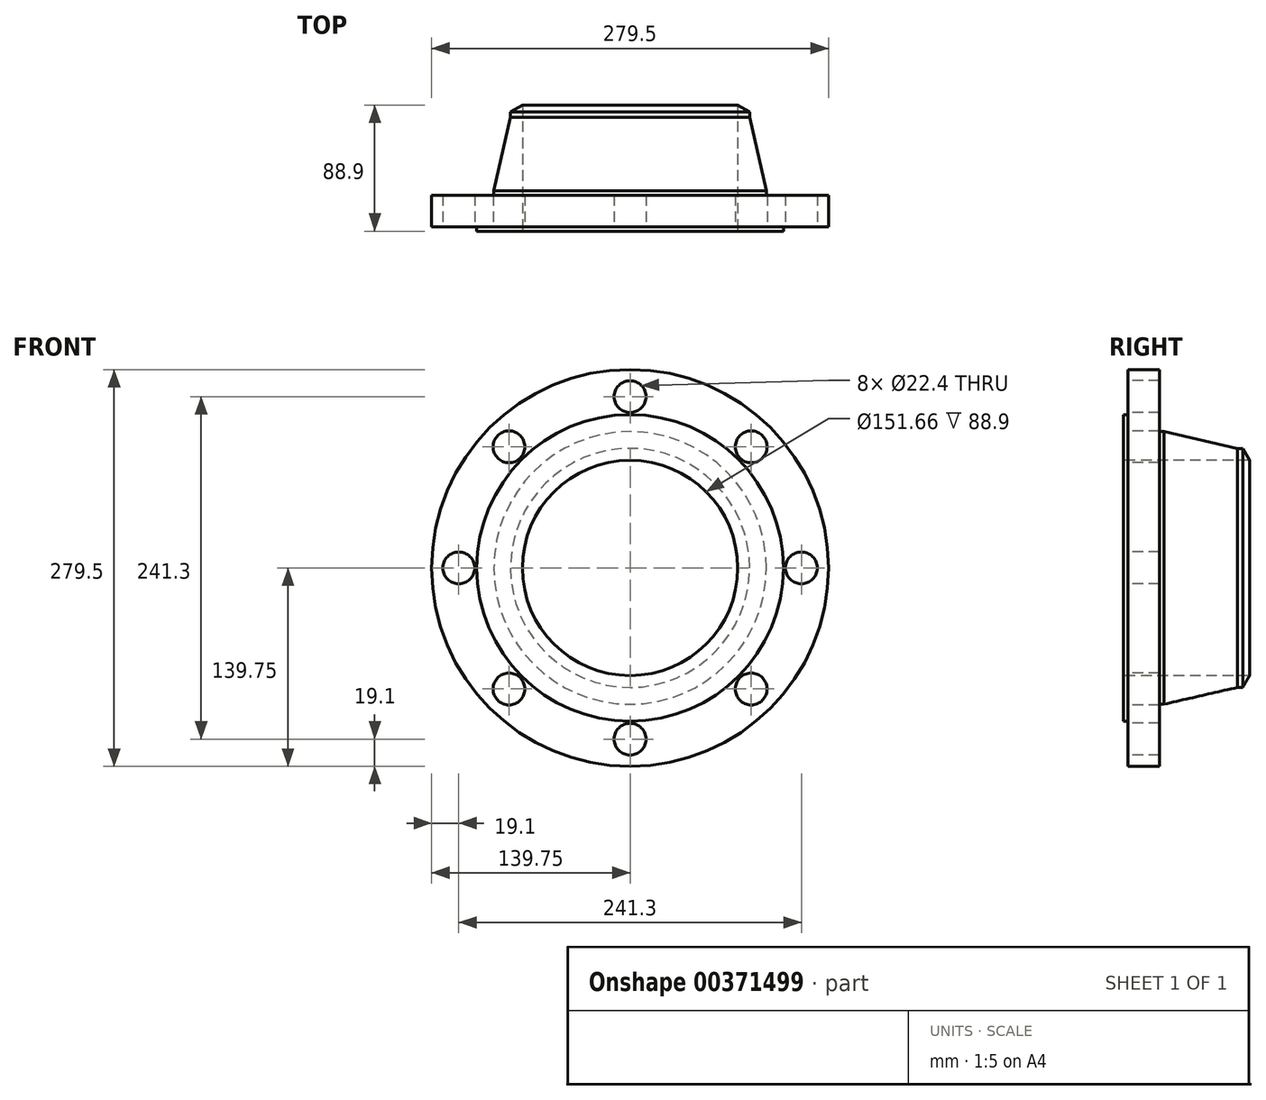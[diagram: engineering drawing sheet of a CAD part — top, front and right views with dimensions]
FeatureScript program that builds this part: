
annotation { "Feature Type Name" : "Feature", "Feature Type Description" : "" }
export const myFeature = defineFeature(function(context is Context, id is Id, definition is map)
    precondition{}
    {
        {
            var Q0;
            Q0=qCreatedBy(makeId("Right.planeOp"),FACE);
            var sketch = newSketch(context, id + "F0", { "sketchPlane" : qUnion([Q0])});
            skLineSegment(sketch, "E0", {"start": v(-100.01, 0) * mm, "end": v(99.5, 0) * mm, "construction": true});
            skLineSegment(sketch, "E1", {"start": v(0, 75.83) * mm, "end": v(0, 107.95) * mm});
            skLineSegment(sketch, "E2", {"start": v(0, 107.95) * mm, "end": v(3.18, 107.95) * mm});
            skLineSegment(sketch, "E3", {"start": v(3.18, 107.95) * mm, "end": v(3.18, 139.75) * mm});
            skLineSegment(sketch, "E4", {"start": v(3.18, 139.75) * mm, "end": v(25.4, 139.75) * mm});
            skLineSegment(sketch, "E5", {"start": v(25.4, 139.75) * mm, "end": v(25.4, 96) * mm});
            skLineSegment(sketch, "E6", {"start": v(25.4, 96) * mm, "end": v(28.58, 96) * mm});
            skLineSegment(sketch, "E7", {"start": v(0, 75.83) * mm, "end": v(88.9, 75.83) * mm});
            skLineSegment(sketch, "E8", {"start": v(88.9, 75.83) * mm, "end": v(84.12, 84.2) * mm});
            skLineSegment(sketch, "E9", {"start": v(84.12, 84.2) * mm, "end": v(80.3, 84.2) * mm});
            skLineSegment(sketch, "E10", {"start": v(80.3, 84.2) * mm, "end": v(28.57, 96) * mm});
            skSolve(sketch);
        }
        {
            var Q0;
            Q0=makeQuery(id+"F0.imprint","IMPRINT",FACE,{"disambiguationData":[TD([[makeQuery(id+"F0.imprint","IMPRINT",EDGE,{"derivedFrom":sQuery(id+"F0.wireOp",EDGE,"E1")}),-1.0]])]});
            var Q1;
            Q1=sQuery(id+"F0.wireOp",EDGE,"E0");
            revolve(context, id + "F1", {"entities" : qUnion([Q0]), "axis" : qUnion([Q1]), "revolveType" : RevolveType.FULL});
        }
        {
            var Q0;
            Q0=makeQuery(id+"F1.opRevolve","SWEPT_FACE",FACE,{"disambiguationData":[OSD([sQuery(id+"F0.wireOp",EDGE,"E3")])]});
            var sketch = newSketch(context, id + "F2", { "sketchPlane" : qUnion([Q0])});
            skCircle(sketch, "E11", {"center": v(0, 120.65) * mm, "radius": 11.2 * mm});
            skCircle(sketch, "E12.1.0", {"center": v(-85.31, 85.31) * mm, "radius": 11.2 * mm});
            skCircle(sketch, "E12.2.0", {"center": v(-120.65, 0) * mm, "radius": 11.2 * mm});
            skCircle(sketch, "E12.3.0", {"center": v(-85.31, -85.31) * mm, "radius": 11.2 * mm});
            skCircle(sketch, "E12.4.0", {"center": v(0, -120.65) * mm, "radius": 11.2 * mm});
            skCircle(sketch, "E12.5.0", {"center": v(85.31, -85.31) * mm, "radius": 11.2 * mm});
            skCircle(sketch, "E12.6.0", {"center": v(120.65, 0) * mm, "radius": 11.2 * mm});
            skCircle(sketch, "E12.7.0", {"center": v(85.31, 85.31) * mm, "radius": 11.2 * mm});
            skPoint(sketch, "E12.center", {"position": v(0, 0) * mm});
            skSolve(sketch);
        }
        {
            var Q0;
            Q0=makeQuery(id+"F2.imprint","IMPRINT",FACE,{"disambiguationData":[TD([[makeQuery(id+"F2.imprint","IMPRINT",EDGE,{"derivedFrom":sQuery(id+"F2.wireOp",EDGE,"E12.1.0")}),1.0]])]});
            var Q1;
            Q1=makeQuery(id+"F2.imprint","IMPRINT",FACE,{"disambiguationData":[TD([[makeQuery(id+"F2.imprint","IMPRINT",EDGE,{"derivedFrom":sQuery(id+"F2.wireOp",EDGE,"E11")}),1.0]])]});
            var Q2;
            Q2=makeQuery(id+"F2.imprint","IMPRINT",FACE,{"disambiguationData":[TD([[makeQuery(id+"F2.imprint","IMPRINT",EDGE,{"derivedFrom":sQuery(id+"F2.wireOp",EDGE,"E12.7.0")}),1.0]])]});
            var Q3;
            Q3=makeQuery(id+"F2.imprint","IMPRINT",FACE,{"disambiguationData":[TD([[makeQuery(id+"F2.imprint","IMPRINT",EDGE,{"derivedFrom":sQuery(id+"F2.wireOp",EDGE,"E12.6.0")}),1.0]])]});
            var Q4;
            Q4=makeQuery(id+"F2.imprint","IMPRINT",FACE,{"disambiguationData":[TD([[makeQuery(id+"F2.imprint","IMPRINT",EDGE,{"derivedFrom":sQuery(id+"F2.wireOp",EDGE,"E12.5.0")}),1.0]])]});
            var Q5;
            Q5=makeQuery(id+"F2.imprint","IMPRINT",FACE,{"disambiguationData":[TD([[makeQuery(id+"F2.imprint","IMPRINT",EDGE,{"derivedFrom":sQuery(id+"F2.wireOp",EDGE,"E12.4.0")}),1.0]])]});
            var Q6;
            Q6=makeQuery(id+"F2.imprint","IMPRINT",FACE,{"disambiguationData":[TD([[makeQuery(id+"F2.imprint","IMPRINT",EDGE,{"derivedFrom":sQuery(id+"F2.wireOp",EDGE,"E12.3.0")}),1.0]])]});
            var Q7;
            Q7=makeQuery(id+"F2.imprint","IMPRINT",FACE,{"disambiguationData":[TD([[makeQuery(id+"F2.imprint","IMPRINT",EDGE,{"derivedFrom":sQuery(id+"F2.wireOp",EDGE,"E12.2.0")}),1.0]])]});
            extrude(context, id + "F3", {"entities" : qUnion([Q0, Q1, Q2, Q3, Q4, Q5, Q6, Q7]), "operationType" : NewBodyOperationType.REMOVE, "endBound" : BoundingType.THROUGH_ALL, "oppositeDirection" : true, "depth" : 25.4 * mm});
        }
    });
